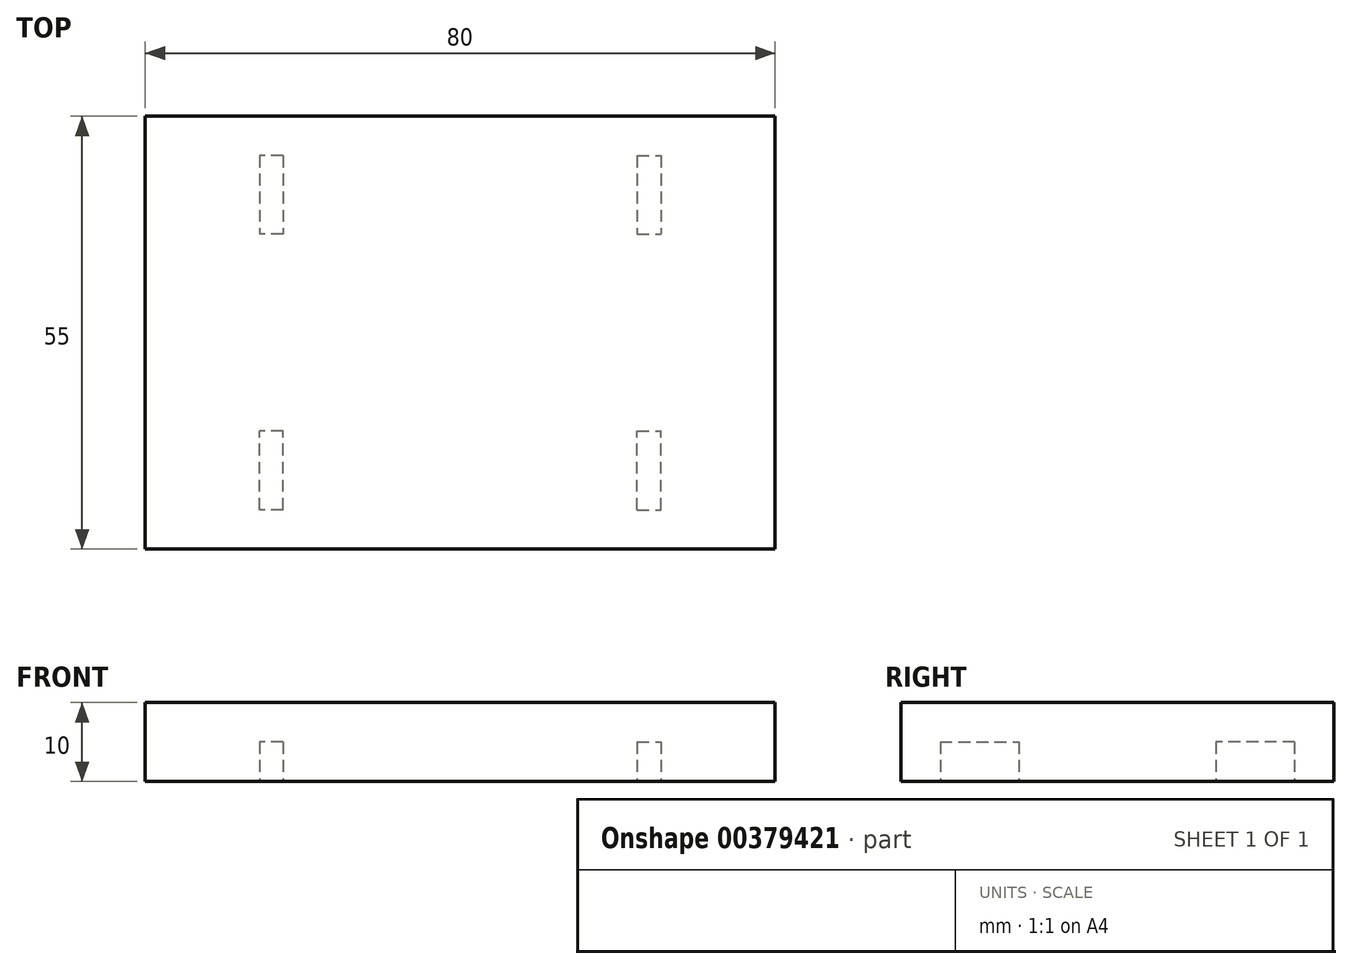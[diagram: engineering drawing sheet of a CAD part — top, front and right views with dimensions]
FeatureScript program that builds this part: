
annotation { "Feature Type Name" : "Feature", "Feature Type Description" : "" }
export const myFeature = defineFeature(function(context is Context, id is Id, definition is map)
    precondition{}
    {
        {
            var Q0;
            Q0=qCreatedBy(makeId("Top.planeOp"),FACE);
            var sketch = newSketch(context, id + "F0", { "sketchPlane" : qUnion([Q0])});
            skLineSegment(sketch, "E0.bottom", {"start": v(40, 27.5) * mm, "end": v(-40, 27.5) * mm});
            skLineSegment(sketch, "E0.top", {"start": v(40, -27.5) * mm, "end": v(-40, -27.5) * mm});
            skLineSegment(sketch, "E0.left", {"start": v(40, 27.5) * mm, "end": v(40, -27.5) * mm});
            skLineSegment(sketch, "E0.right", {"start": v(-40, 27.5) * mm, "end": v(-40, -27.5) * mm});
            skPoint(sketch, "E0.middle", {"position": v(0, 0) * mm});
            skSolve(sketch);
        }
        {
            var Q0;
            Q0 = qSketchRegion(id + "F0", true);
            extrude(context, id + "F1", {"entities" : qUnion([Q0]), "depth" : 10 * mm});
        }
        {
            var Q0;
            Q0=makeQuery(id+"F1.opExtrude","CAP_FACE",FACE,{"disambiguationData":[OSD([sQuery(id+"F0.wireOp",EDGE,"E0.bottom"),sQuery(id+"F0.wireOp",EDGE,"E0.top"),sQuery(id+"F0.wireOp",EDGE,"E0.left"),sQuery(id+"F0.wireOp",EDGE,"E0.right")])],"isStart":true});
            var sketch = newSketch(context, id + "F2", { "sketchPlane" : qUnion([Q0])});
            skLineSegment(sketch, "E1", {"start": v(0, 27.5) * mm, "end": v(-22.5, 27.5) * mm, "construction": true});
            skLineSegment(sketch, "E2", {"start": v(-22.5, 27.5) * mm, "end": v(-22.5, 22.5) * mm, "construction": true});
            skLineSegment(sketch, "E3.bottom", {"start": v(-22.5, 22.5) * mm, "end": v(-25.5, 22.5) * mm});
            skLineSegment(sketch, "E3.top", {"start": v(-22.5, 12.5) * mm, "end": v(-25.5, 12.5) * mm});
            skLineSegment(sketch, "E3.left", {"start": v(-22.5, 22.5) * mm, "end": v(-22.5, 12.5) * mm});
            skLineSegment(sketch, "E3.right", {"start": v(-25.5, 22.5) * mm, "end": v(-25.5, 12.5) * mm});
            skLineSegment(sketch, "E4", {"start": v(0, 27.5) * mm, "end": v(0, 0) * mm, "construction": true});
            skLineSegment(sketch, "E5", {"start": v(0, 0) * mm, "end": v(40, 0) * mm, "construction": true});
            skLineSegment(sketch, "E6.MirrorCS", {"start": v(22.5, 22.5) * mm, "end": v(22.5, 12.5) * mm});
            skLineSegment(sketch, "E7.MirrorCS", {"start": v(25.5, 22.5) * mm, "end": v(25.5, 12.5) * mm});
            skLineSegment(sketch, "E8.MirrorCS", {"start": v(22.5, 22.5) * mm, "end": v(25.5, 22.5) * mm});
            skLineSegment(sketch, "E9.MirrorCS", {"start": v(22.5, 12.5) * mm, "end": v(25.5, 12.5) * mm});
            skLineSegment(sketch, "E10.MirrorCS", {"start": v(-22.5, -22.5) * mm, "end": v(-25.5, -22.5) * mm});
            skLineSegment(sketch, "E11.MirrorCS", {"start": v(-22.5, -12.5) * mm, "end": v(-25.5, -12.5) * mm});
            skLineSegment(sketch, "E12.MirrorCS", {"start": v(22.5, -22.5) * mm, "end": v(25.5, -22.5) * mm});
            skLineSegment(sketch, "E13.MirrorCS", {"start": v(22.5, -12.5) * mm, "end": v(25.5, -12.5) * mm});
            skLineSegment(sketch, "E14.MirrorCS", {"start": v(-25.5, -22.5) * mm, "end": v(-25.5, -12.5) * mm});
            skLineSegment(sketch, "E15.MirrorCS", {"start": v(-22.5, -22.5) * mm, "end": v(-22.5, -12.5) * mm});
            skLineSegment(sketch, "E16.MirrorCS", {"start": v(22.5, -22.5) * mm, "end": v(22.5, -12.5) * mm});
            skLineSegment(sketch, "E17.MirrorCS", {"start": v(25.5, -22.5) * mm, "end": v(25.5, -12.5) * mm});
            skSolve(sketch);
        }
        {
            var Q0;
            Q0 = qSketchRegion(id + "F2", true);
            extrude(context, id + "F3", {"entities" : qUnion([Q0]), "operationType" : NewBodyOperationType.REMOVE, "oppositeDirection" : true, "depth" : 5 * mm});
        }
    });
